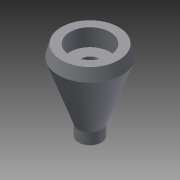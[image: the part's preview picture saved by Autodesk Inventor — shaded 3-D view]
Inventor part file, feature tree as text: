
AUTODESK INVENTOR PART (.ipt)
format: ipt  version: 2015 (Build 190159000, 159)  size: 103,424 bytes
history: native  units: in
note: dims shown in document units (in); Inventor stores cm internally (conversion verified against a paired STEP export)
features: sketch x2, revolve x1, hole x1, chamfer x1
ambient origin geometry x8: Origin, YZ Plane, XZ Plane, XY Plane, X Axis, Y Axis, Z Axis, Center Point
bodies: Solid1 (feature_tree)
feature tree (5):
  revolve  "Revolution1"  [1 undecoded]
  hole  "Hole1"  [1 undecoded]
  chamfer  "Chamfer1"  Distance=1.5in
  sketch  "Sketch1"  dims[d0=0.25in d1=0.25in]
  sketch  "Sketch2"  dims[d2=1.75in d3=75.0deg d4=1.5in d5=90.0deg d6=0.375in d7=0.75in d8=0.875in d9=0.375in d10=0.5635in d11=1.5in d12=0.8108in d13=0.01in d14=0.125in d15=45.0deg]
note: 2 required parameter values undecoded (feature->parameter linkage not recoverable at this tier; creation-order binding heuristic only, values carry confidence <= 0.55)